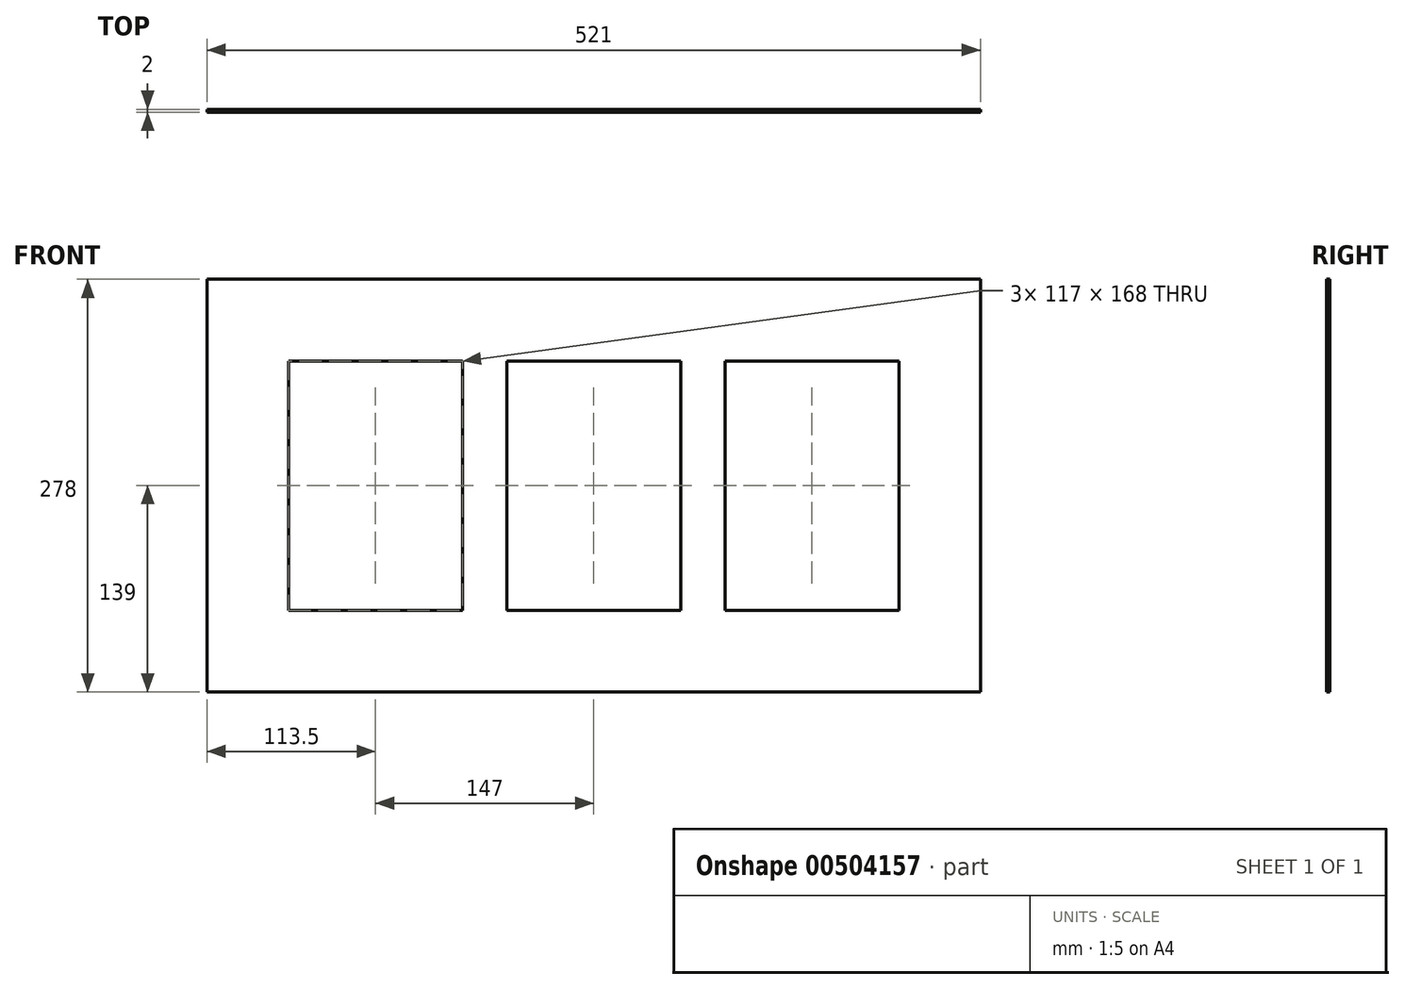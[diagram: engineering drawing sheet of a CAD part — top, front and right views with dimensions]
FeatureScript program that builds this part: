
annotation { "Feature Type Name" : "Feature", "Feature Type Description" : "" }
export const myFeature = defineFeature(function(context is Context, id is Id, definition is map)
    precondition{}
    {
        {
            var Q0;
            Q0=qCreatedBy(makeId("Front.planeOp"),FACE);
            var sketch = newSketch(context, id + "F0", { "sketchPlane" : qUnion([Q0])});
            skLineSegment(sketch, "E0.bottom", {"start": v(260.5, -139) * mm, "end": v(-260.5, -139) * mm});
            skLineSegment(sketch, "E0.top", {"start": v(260.5, 139) * mm, "end": v(-260.5, 139) * mm});
            skLineSegment(sketch, "E0.left", {"start": v(260.5, -139) * mm, "end": v(260.5, 139) * mm});
            skLineSegment(sketch, "E0.right", {"start": v(-260.5, -139) * mm, "end": v(-260.5, 139) * mm});
            skPoint(sketch, "E0.middle", {"position": v(0, 0) * mm});
            skLineSegment(sketch, "E1", {"start": v(-260.5, 0) * mm, "end": v(260.5, 0) * mm, "construction": true});
            skLineSegment(sketch, "E2.bottom", {"start": v(63.5, -89) * mm, "end": v(-63.5, -89) * mm, "construction": true});
            skLineSegment(sketch, "E2.top", {"start": v(63.5, 89) * mm, "end": v(-63.5, 89) * mm, "construction": true});
            skLineSegment(sketch, "E2.left", {"start": v(63.5, -89) * mm, "end": v(63.5, 89) * mm, "construction": true});
            skLineSegment(sketch, "E2.right", {"start": v(-63.5, -89) * mm, "end": v(-63.5, 89) * mm, "construction": true});
            skLineSegment(sketch, "E3.bottom", {"start": v(58.5, -84) * mm, "end": v(-58.5, -84) * mm});
            skLineSegment(sketch, "E3.top", {"start": v(58.5, 84) * mm, "end": v(-58.5, 84) * mm});
            skLineSegment(sketch, "E3.left", {"start": v(58.5, -84) * mm, "end": v(58.5, 84) * mm});
            skLineSegment(sketch, "E3.right", {"start": v(-58.5, -84) * mm, "end": v(-58.5, 84) * mm});
            skLineSegment(sketch, "E4.bottom", {"start": v(210.5, -89) * mm, "end": v(83.5, -89) * mm, "construction": true});
            skLineSegment(sketch, "E4.top", {"start": v(210.5, 89) * mm, "end": v(83.5, 89) * mm, "construction": true});
            skLineSegment(sketch, "E4.left", {"start": v(210.5, -89) * mm, "end": v(210.5, 89) * mm, "construction": true});
            skLineSegment(sketch, "E4.right", {"start": v(83.5, -89) * mm, "end": v(83.5, 89) * mm, "construction": true});
            skPoint(sketch, "E4.middle", {"position": v(147, 0) * mm});
            skLineSegment(sketch, "E5.bottom", {"start": v(205.5, 84) * mm, "end": v(88.5, 84) * mm});
            skLineSegment(sketch, "E5.top", {"start": v(205.5, -84) * mm, "end": v(88.5, -84) * mm});
            skLineSegment(sketch, "E5.left", {"start": v(205.5, 84) * mm, "end": v(205.5, -84) * mm});
            skLineSegment(sketch, "E5.right", {"start": v(88.5, 84) * mm, "end": v(88.5, -84) * mm});
            skLineSegment(sketch, "E6.MirrorCS", {"start": v(-205.5, -84) * mm, "end": v(-88.5, -84) * mm});
            skLineSegment(sketch, "E7.MirrorCS", {"start": v(-205.5, 84) * mm, "end": v(-205.5, -84) * mm});
            skLineSegment(sketch, "E8.MirrorCS", {"start": v(-205.5, 84) * mm, "end": v(-88.5, 84) * mm});
            skLineSegment(sketch, "E9.MirrorCS", {"start": v(-88.5, 84) * mm, "end": v(-88.5, -84) * mm});
            skSolve(sketch);
        }
        {
            var Q0;
            Q0=makeQuery(id+"F0.imprint","IMPRINT",FACE,{"disambiguationData":[TD([[makeQuery(id+"F0.imprint","IMPRINT",EDGE,{"derivedFrom":sQuery(id+"F0.wireOp",EDGE,"E0.bottom")}),-1.0]])]});
            extrude(context, id + "F1", {"entities" : qUnion([Q0]), "depth" : 2 * mm, "offsetDistance" : 25 * mm});
        }
    });
